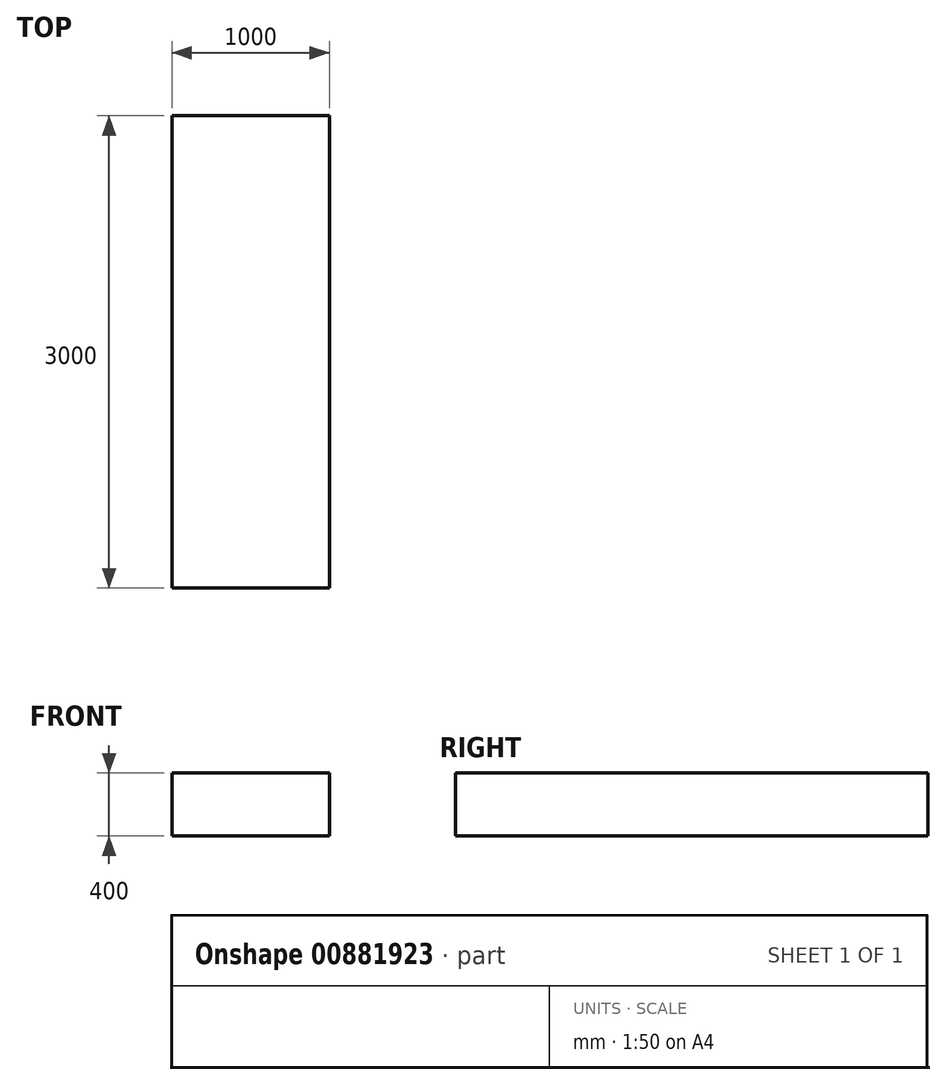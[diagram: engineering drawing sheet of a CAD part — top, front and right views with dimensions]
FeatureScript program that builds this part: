
annotation { "Feature Type Name" : "Feature", "Feature Type Description" : "" }
export const myFeature = defineFeature(function(context is Context, id is Id, definition is map)
    precondition{}
    {
        {
            var Q0;
            Q0=qCreatedBy(makeId("Top.planeOp"),FACE);
            var sketch = newSketch(context, id + "F0", { "sketchPlane" : qUnion([Q0])});
            skLineSegment(sketch, "E0.bottom", {"start": v(-572.42, -1465.37) * mm, "end": v(427.58, -1465.37) * mm});
            skLineSegment(sketch, "E0.top", {"start": v(-572.42, 1534.63) * mm, "end": v(427.58, 1534.63) * mm});
            skLineSegment(sketch, "E0.left", {"start": v(-572.42, -1465.37) * mm, "end": v(-572.42, 1534.63) * mm});
            skLineSegment(sketch, "E0.right", {"start": v(427.58, -1465.37) * mm, "end": v(427.58, 1534.63) * mm});
            skSolve(sketch);
        }
        {
            var Q0;
            Q0=makeQuery(id+"F0.imprint","IMPRINT",FACE,{"disambiguationData":[TD([[makeQuery(id+"F0.imprint","IMPRINT",EDGE,{"derivedFrom":sQuery(id+"F0.wireOp",EDGE,"E0.bottom")}),1.0]])]});
            extrude(context, id + "F1", {"entities" : qUnion([Q0]), "depth" : 400 * mm, "offsetDistance" : 25 * mm});
        }
    });
